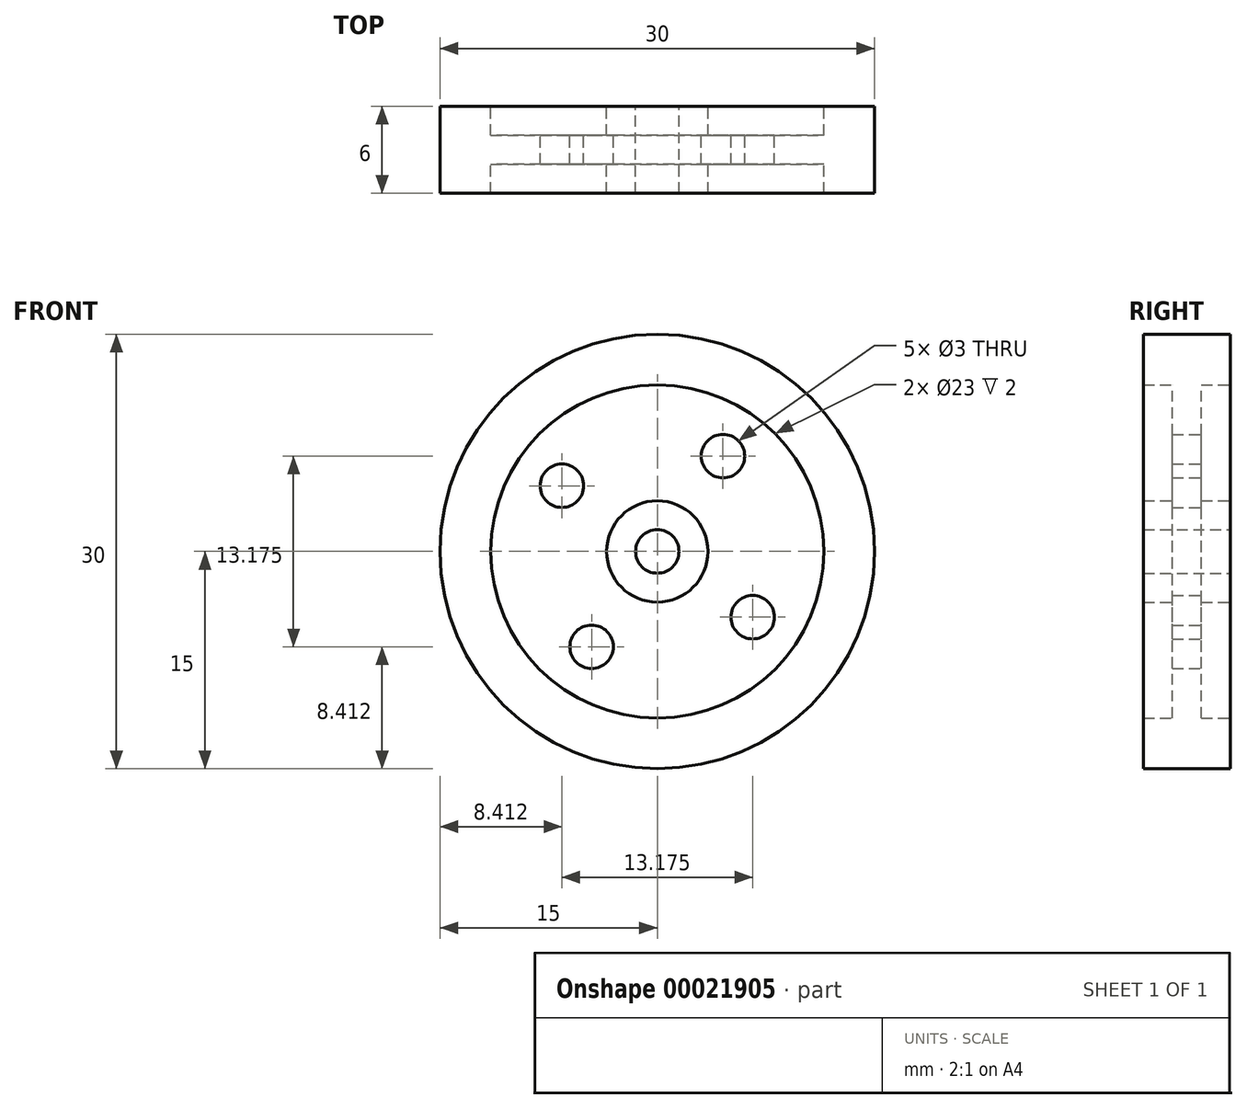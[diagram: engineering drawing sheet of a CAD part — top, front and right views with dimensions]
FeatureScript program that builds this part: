
annotation { "Feature Type Name" : "Feature", "Feature Type Description" : "" }
export const myFeature = defineFeature(function(context is Context, id is Id, definition is map)
    precondition{}
    {
        {
            var Q0;
            Q0=qCreatedBy(makeId("Front.planeOp"),FACE);
            var sketch = newSketch(context, id + "F0", { "sketchPlane" : qUnion([Q0])});
            skCircle(sketch, "E0", {"center": v(0, 0) * mm, "radius": 11.5 * mm});
            skCircle(sketch, "E1", {"center": v(0, 0) * mm, "radius": 15 * mm});
            skCircle(sketch, "E2", {"center": v(0, 0) * mm, "radius": 3.5 * mm});
            skCircle(sketch, "E3", {"center": v(0, 0) * mm, "radius": 1.5 * mm});
            skCircle(sketch, "E4", {"center": v(4.54, 6.59) * mm, "radius": 1.5 * mm});
            skCircle(sketch, "E5.1.0", {"center": v(-6.59, 4.54) * mm, "radius": 1.5 * mm});
            skCircle(sketch, "E5.2.0", {"center": v(-4.54, -6.59) * mm, "radius": 1.5 * mm});
            skCircle(sketch, "E5.3.0", {"center": v(6.59, -4.54) * mm, "radius": 1.5 * mm});
            skSolve(sketch);
        }
        {
            var Q0;
            Q0=qSketchRegion(id+"F0",true);
            var Q1;
            Q1=makeQuery(id+"F0.imprint","IMPRINT",FACE,{"disambiguationData":[TD([[makeQuery(id+"F0.imprint","IMPRINT",EDGE,{"derivedFrom":sQuery(id+"F0.wireOp",EDGE,"E2")}),1.0]])]});
            extrude(context, id + "F1", {"entities" : qUnion([Q0, Q1]), "depth" : 6 * mm});
        }
        {
            var Q0;
            Q0=makeQuery(id+"F0.imprint","IMPRINT",FACE,{"disambiguationData":[TD([[makeQuery(id+"F0.imprint","IMPRINT",EDGE,{"derivedFrom":sQuery(id+"F0.wireOp",EDGE,"E0")}),1.0]])]});
            extrude(context, id + "F2", {"entities" : qUnion([Q0]), "operationType" : NewBodyOperationType.ADD, "depth" : 4 * mm});
        }
        {
            var Q0;
            Q0=makeQuery(id+"F0.imprint","IMPRINT",FACE,{"disambiguationData":[TD([[makeQuery(id+"F0.imprint","IMPRINT",EDGE,{"derivedFrom":sQuery(id+"F0.wireOp",EDGE,"E0")}),1.0]])]});
            extrude(context, id + "F3", {"entities" : qUnion([Q0]), "operationType" : NewBodyOperationType.REMOVE, "depth" : 2 * mm});
        }
    });
